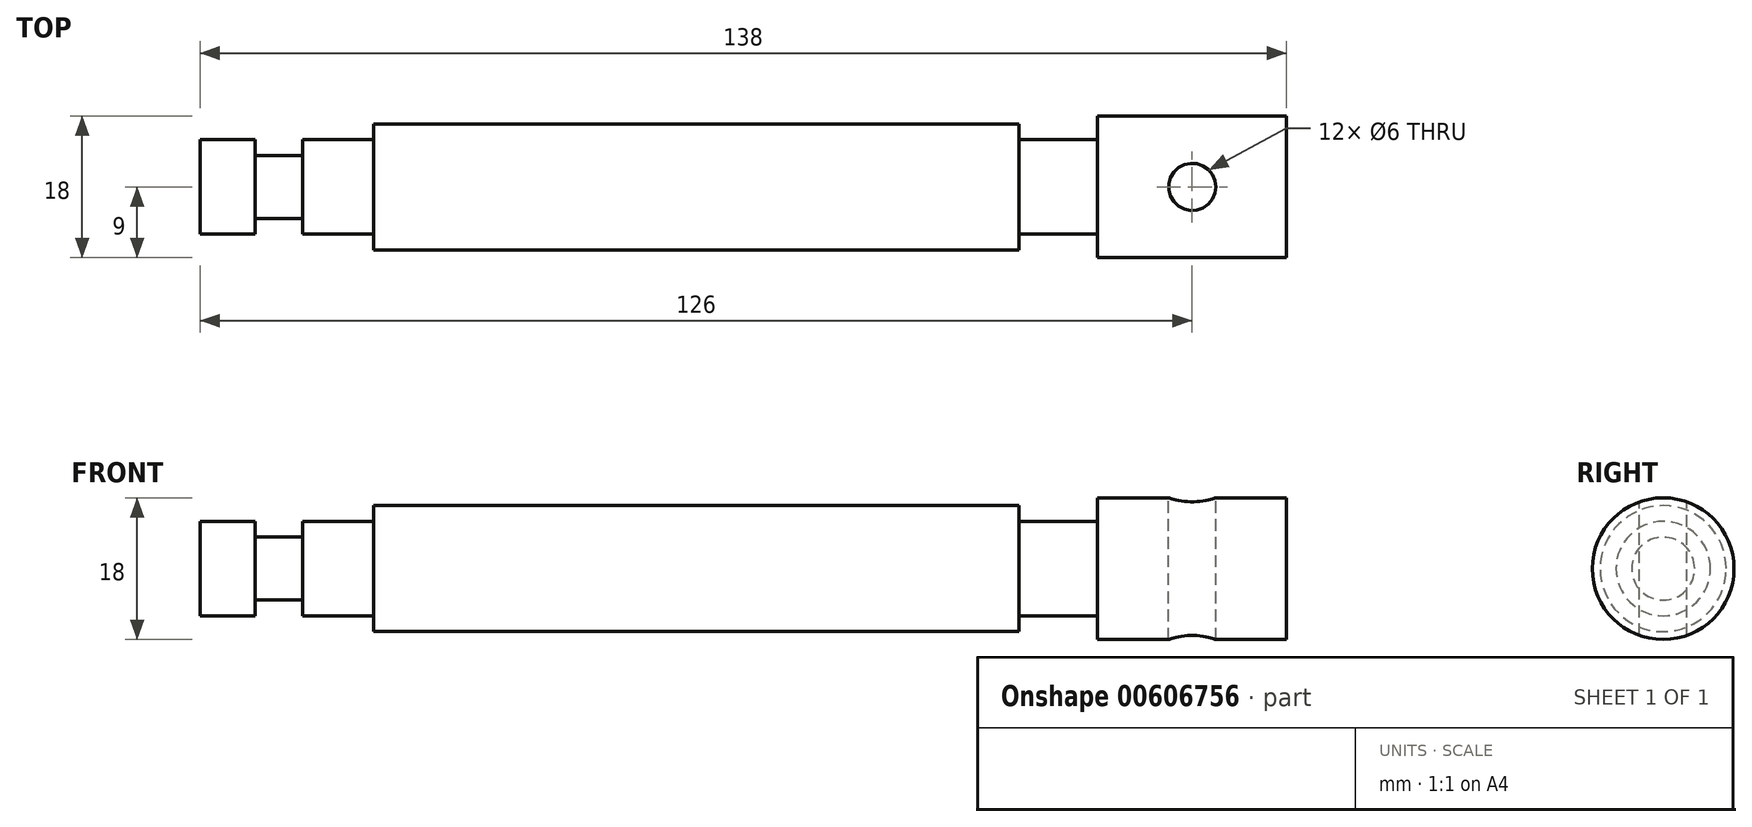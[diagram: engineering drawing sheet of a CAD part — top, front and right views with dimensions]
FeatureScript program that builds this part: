
annotation { "Feature Type Name" : "Feature", "Feature Type Description" : "" }
export const myFeature = defineFeature(function(context is Context, id is Id, definition is map)
    precondition{}
    {
        {
            var Q0;
            Q0=qCreatedBy(makeId("Front.planeOp"),FACE);
            var sketch = newSketch(context, id + "F0", { "sketchPlane" : qUnion([Q0])});
            skLineSegment(sketch, "E0", {"start": v(0, 0) * mm, "end": v(0, 6) * mm});
            skLineSegment(sketch, "E1", {"start": v(0, 6) * mm, "end": v(7, 6) * mm});
            skLineSegment(sketch, "E2", {"start": v(7, 6) * mm, "end": v(7, 4) * mm});
            skLineSegment(sketch, "E3", {"start": v(7, 4) * mm, "end": v(13, 4) * mm});
            skLineSegment(sketch, "E4", {"start": v(13, 4) * mm, "end": v(13, 6) * mm});
            skLineSegment(sketch, "E5", {"start": v(13, 6) * mm, "end": v(22, 6) * mm});
            skLineSegment(sketch, "E6", {"start": v(22, 6) * mm, "end": v(22, 8) * mm});
            skLineSegment(sketch, "E7", {"start": v(22, 8) * mm, "end": v(104, 8) * mm});
            skLineSegment(sketch, "E8", {"start": v(104, 8) * mm, "end": v(104, 6) * mm});
            skLineSegment(sketch, "E9", {"start": v(104, 6) * mm, "end": v(114, 6) * mm});
            skLineSegment(sketch, "E10", {"start": v(114, 6) * mm, "end": v(114, 9) * mm});
            skLineSegment(sketch, "E11", {"start": v(114, 9) * mm, "end": v(138, 9) * mm});
            skLineSegment(sketch, "E12", {"start": v(138, 9) * mm, "end": v(138, 0) * mm});
            skLineSegment(sketch, "E13", {"start": v(138, 0) * mm, "end": v(0, 0) * mm});
            skSolve(sketch);
        }
        {
            var Q0;
            Q0=makeQuery(id+"F0.imprint","IMPRINT",FACE,{"disambiguationData":[TD([[makeQuery(id+"F0.imprint","IMPRINT",EDGE,{"derivedFrom":sQuery(id+"F0.wireOp",EDGE,"E0")}),-1.0]])]});
            var Q1;
            Q1=sQuery(id+"F0.wireOp",EDGE,"E13");
            revolve(context, id + "F1", {"entities" : qUnion([Q0]), "axis" : qUnion([Q1]), "revolveType" : RevolveType.FULL});
        }
        {
            var Q0;
            Q0=qCreatedBy(makeId("Top.planeOp"),FACE);
            var sketch = newSketch(context, id + "F2", { "sketchPlane" : qUnion([Q0])});
            skCircle(sketch, "E14", {"center": v(126, 0) * mm, "radius": 3 * mm});
            skSolve(sketch);
        }
        {
            var Q0;
            Q0 = qSketchRegion(id + "F2", true);
            extrude(context, id + "F3", {"entities" : qUnion([Q0]), "operationType" : NewBodyOperationType.REMOVE, "endBound" : BoundingType.THROUGH_ALL, "oppositeDirection" : true, "depth" : 25 * mm, "offsetDistance" : 25 * mm, "hasSecondDirection" : true, "secondDirectionBound" : SecondDirectionBoundingType.THROUGH_ALL, "secondDirectionOppositeDirection" : false, "secondDirectionDepth" : 25 * mm});
        }
    });
